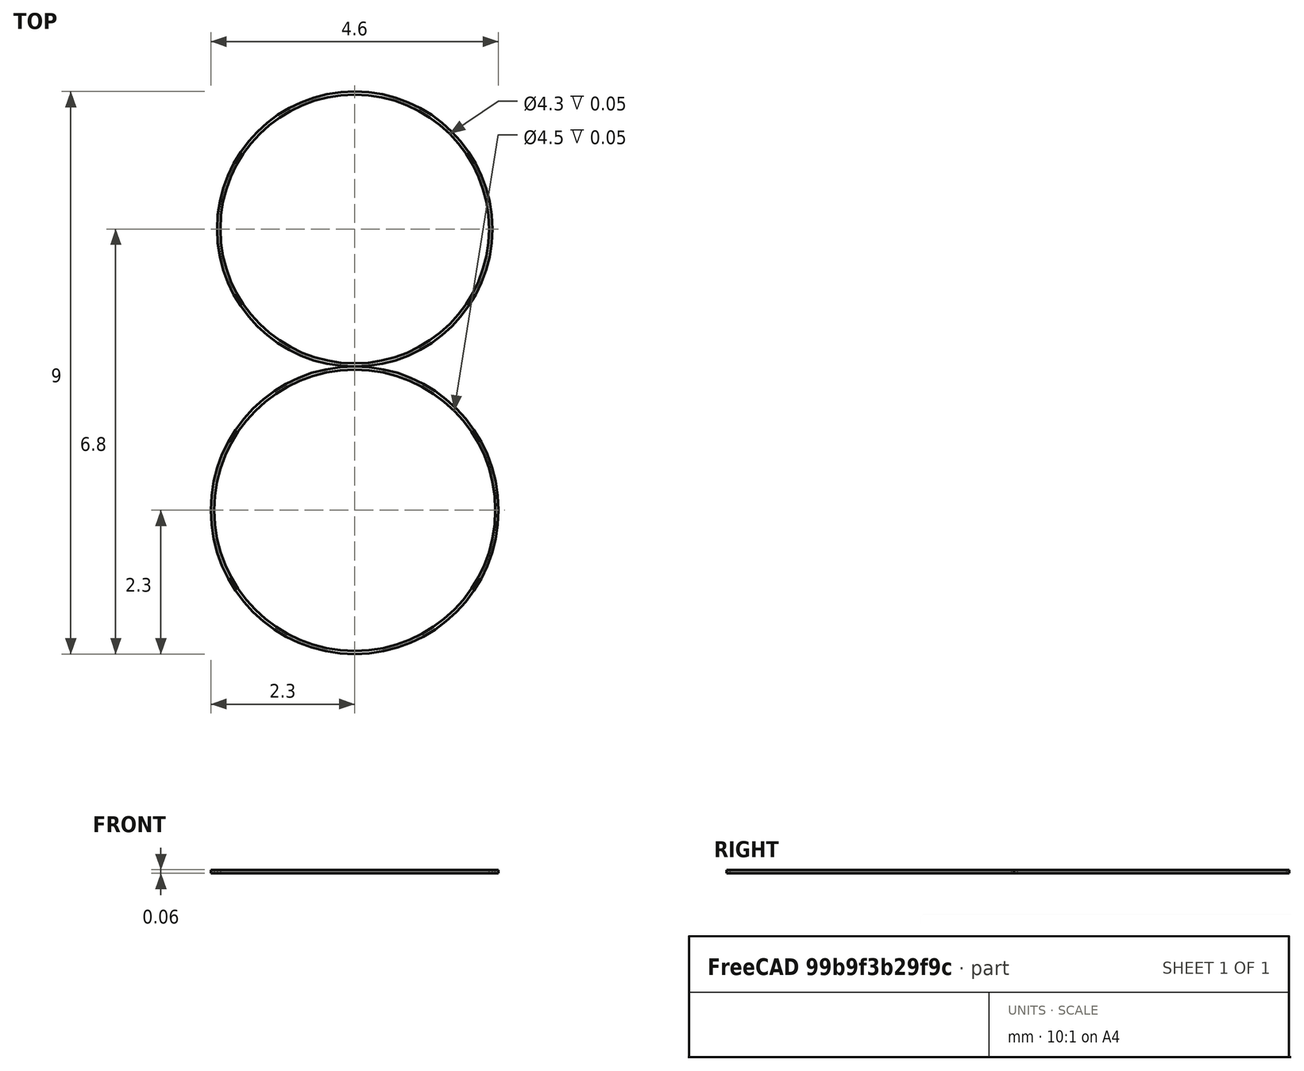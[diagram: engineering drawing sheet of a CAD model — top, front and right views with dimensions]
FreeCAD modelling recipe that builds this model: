
FCSTD DOCUMENT  (FreeCAD 0.16R6712 (Git))
Label: 8t
License: All rights reserved
LicenseURL: http://en.wikipedia.org/wiki/All_rights_reserved
objects: Sketcher::SketchObject×2, PartDesign::Pad×2, Part::MultiFuse×1, Mesh::Feature×1
note: 7 computed .brp shape members not serialized (recipe doc carries the construction recipe); baked Part::Feature solids carry a one-line shape summary decoded from their .brp

FEATURE [Sketcher::SketchObject] Sketch
  sketch-geometry (2):
    g0: Circle CenterX=0 CenterY=2.3 CenterZ=0 NormalX=0 NormalY=0 NormalZ=1 Radius=2.25
    g1: Circle CenterX=0 CenterY=2.3 CenterZ=0 NormalX=0 NormalY=0 NormalZ=1 Radius=2.3
  constraints (5):
    c: Coincident(g1,g0)
    c: Radius(g1) = 2.3
    c: Radius(g0) = 2.25
    c: Tangent(g1,g-1)
    c: PointOnObject(g0,g-2)
FEATURE [PartDesign::Pad] Pad
  Length = 0.05
  Length2 = 100
  Midplane = true
  Sketch = -> Sketch
  Type = 0
FEATURE [Sketcher::SketchObject] Sketch001
  sketch-geometry (2):
    g0: Circle CenterX=0 CenterY=6.8 CenterZ=0 NormalX=0 NormalY=0 NormalZ=1 Radius=2.15
    g1: Circle CenterX=0 CenterY=6.8 CenterZ=0 NormalX=0 NormalY=0 NormalZ=1 Radius=2.2
  constraints (5):
    c: Coincident(g1,g0)
    c: PointOnObject(g0,g-2)
    c: Radius(g0) = 2.15
    c: Radius(g1) = 2.2
    c: DistanceY(g-1,g0) = 6.8
FEATURE [PartDesign::Pad] Pad001
  Length = 0.05
  Length2 = 100
  Midplane = true
  Sketch = -> Sketch001
  Type = 0
FEATURE [Part::MultiFuse] Fusion
  Shapes = -> [Pad001,Pad]
FEATURE [Mesh::Feature] Mesh  label="Fusion (Meshed)"
